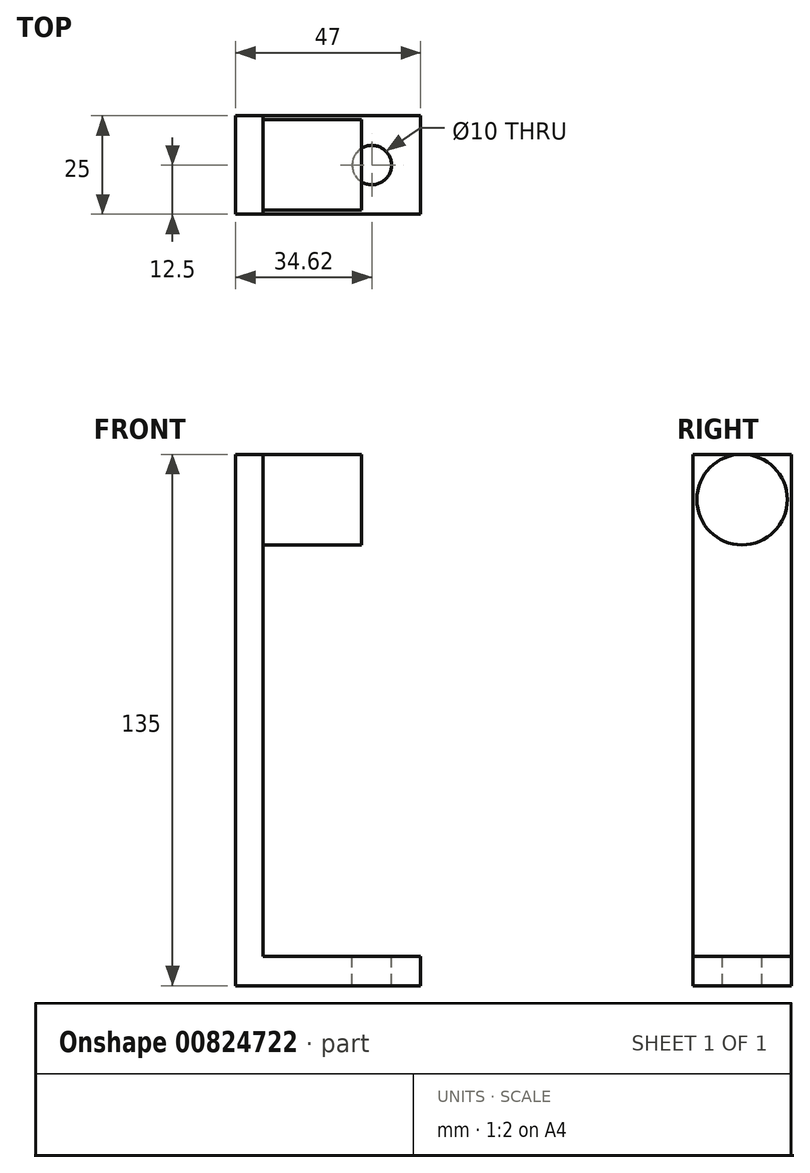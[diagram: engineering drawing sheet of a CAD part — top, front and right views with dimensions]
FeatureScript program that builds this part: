
annotation { "Feature Type Name" : "Feature", "Feature Type Description" : "" }
export const myFeature = defineFeature(function(context is Context, id is Id, definition is map)
    precondition{}
    {
        {
            var Q0;
            Q0=qCreatedBy(makeId("Front.planeOp"),FACE);
            var sketch = newSketch(context, id + "F0", { "sketchPlane" : qUnion([Q0])});
            skLineSegment(sketch, "E0.bottom", {"start": v(-34.62, 75.75) * mm, "end": v(-27.62, 75.75) * mm});
            skLineSegment(sketch, "E0.top", {"start": v(-34.62, -59.25) * mm, "end": v(-27.62, -59.25) * mm});
            skLineSegment(sketch, "E0.left", {"start": v(-34.62, 75.75) * mm, "end": v(-34.62, -59.25) * mm});
            skLineSegment(sketch, "E0.right", {"start": v(-27.62, 75.75) * mm, "end": v(-27.62, -59.25) * mm});
            skSolve(sketch);
        }
        {
            var Q0;
            Q0=makeQuery(id+"F0.imprint","IMPRINT",FACE,{"disambiguationData":[TD([[makeQuery(id+"F0.imprint","IMPRINT",EDGE,{"derivedFrom":sQuery(id+"F0.wireOp",EDGE,"E0.bottom")}),-1.0]])]});
            extrude(context, id + "F1", {"entities" : qUnion([Q0]), "depth" : 25 * mm, "offsetDistance" : 25 * mm});
        }
        {
            var Q0;
            Q0=makeQuery(id+"F1.opExtrude","SWEPT_FACE",FACE,{"disambiguationData":[OSD([sQuery(id+"F0.wireOp",EDGE,"E0.right")])]});
            var sketch = newSketch(context, id + "F2", { "sketchPlane" : qUnion([Q0])});
            skCircle(sketch, "E1", {"center": v(-12.5, 64.25) * mm, "radius": 11.5 * mm});
            skSolve(sketch);
        }
        {
            var Q0;
            Q0=makeQuery(id+"F2.imprint","IMPRINT",FACE,{"disambiguationData":[TD([[makeQuery(id+"F2.imprint","IMPRINT",EDGE,{"derivedFrom":sQuery(id+"F2.wireOp",EDGE,"E1")}),1.0]])]});
            extrude(context, id + "F3", {"entities" : qUnion([Q0]), "operationType" : NewBodyOperationType.ADD, "depth" : 25 * mm, "offsetDistance" : 25 * mm});
        }
        {
            var Q0;
            Q0=makeQuery(id+"F1.opExtrude","SWEPT_FACE",FACE,{"disambiguationData":[OSD([sQuery(id+"F0.wireOp",EDGE,"E0.right")])]});
            var sketch = newSketch(context, id + "F4", { "sketchPlane" : qUnion([Q0])});
            skLineSegment(sketch, "E2.bottom", {"start": v(-25, -59.25) * mm, "end": v(0, -59.25) * mm});
            skLineSegment(sketch, "E2.top", {"start": v(-25, -51.75) * mm, "end": v(0, -51.75) * mm});
            skLineSegment(sketch, "E2.left", {"start": v(-25, -59.25) * mm, "end": v(-25, -51.75) * mm});
            skLineSegment(sketch, "E2.right", {"start": v(0, -59.25) * mm, "end": v(0, -51.75) * mm});
            skSolve(sketch);
        }
        {
            var Q0;
            Q0 = qSketchRegion(id + "F4", true);
            extrude(context, id + "F5", {"entities" : qUnion([Q0]), "operationType" : NewBodyOperationType.ADD, "depth" : 40 * mm, "offsetDistance" : 25 * mm});
        }
        {
            var Q0;
            Q0=makeQuery(id+"F5.opExtrude","SWEPT_FACE",FACE,{"disambiguationData":[OSD([sQuery(id+"F4.wireOp",EDGE,"E2.top")])]});
            var sketch = newSketch(context, id + "F6", { "sketchPlane" : qUnion([Q0])});
            skLineSegment(sketch, "E3.bottom", {"start": v(-6.61, -10) * mm, "end": v(5.97, -10) * mm});
            skLineSegment(sketch, "E3.top", {"start": v(-6.61, -15) * mm, "end": v(5.97, -15) * mm});
            skLineSegment(sketch, "E3.left", {"start": v(-6.61, -10) * mm, "end": v(-6.61, -15) * mm});
            skLineSegment(sketch, "E3.right", {"start": v(5.97, -10) * mm, "end": v(5.97, -15) * mm});
            skSolve(sketch);
        }
        {
            var Q0;
            Q0=makeQuery(id+"F5.opExtrude","SWEPT_FACE",FACE,{"disambiguationData":[OSD([sQuery(id+"F4.wireOp",EDGE,"E2.top")])]});
            var sketch = newSketch(context, id + "F7", { "sketchPlane" : qUnion([Q0])});
            skCircle(sketch, "E4", {"center": v(0, -12.5) * mm, "radius": 5 * mm});
            skSolve(sketch);
        }
        {
            var Q0;
            Q0 = qSketchRegion(id + "F7", true);
            extrude(context, id + "F8", {"entities" : qUnion([Q0]), "operationType" : NewBodyOperationType.REMOVE, "endBound" : BoundingType.THROUGH_ALL, "oppositeDirection" : true, "depth" : 25 * mm, "offsetDistance" : 25 * mm});
        }
    });
